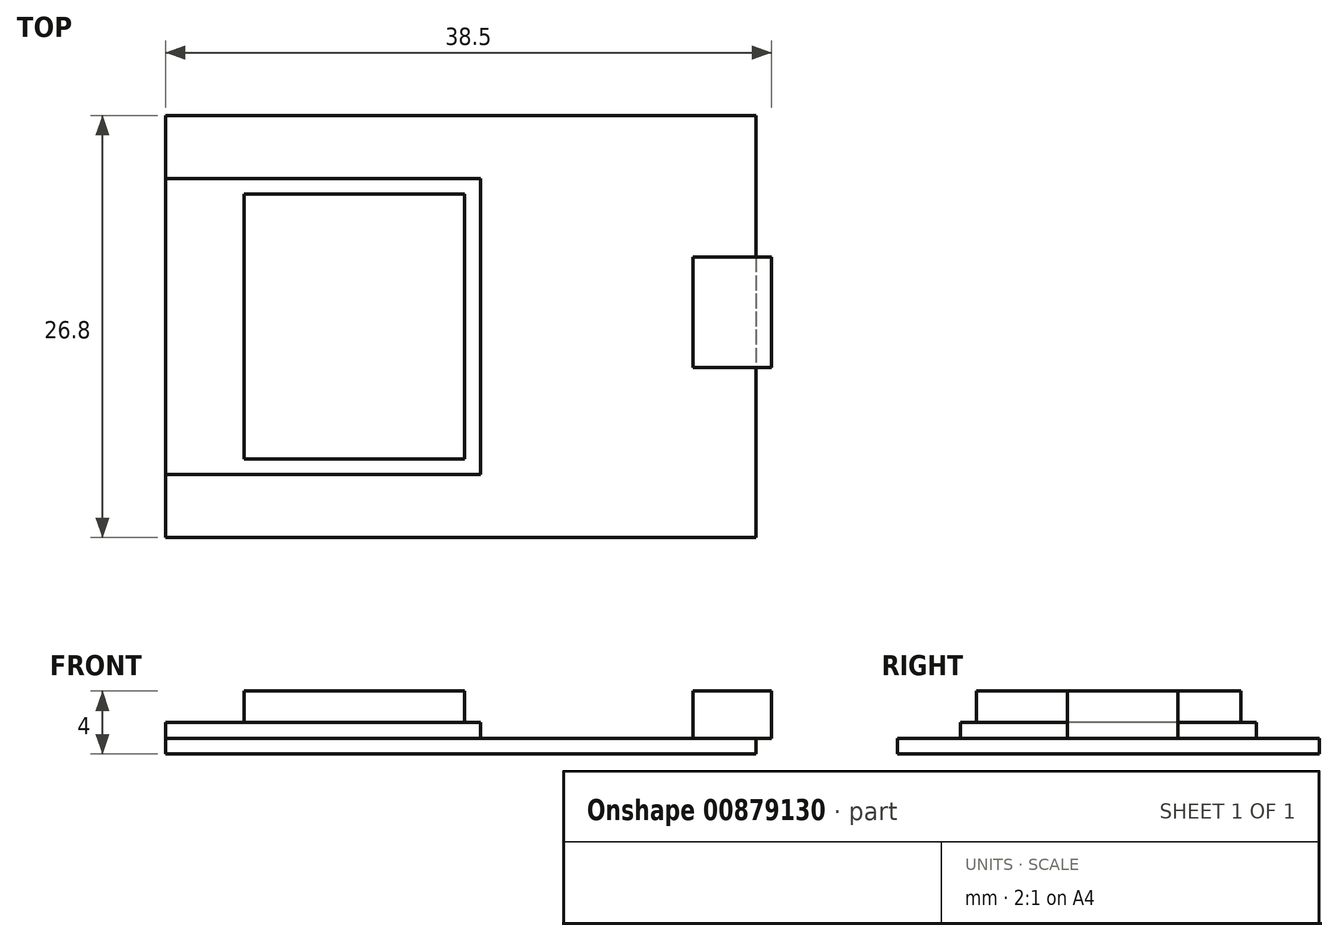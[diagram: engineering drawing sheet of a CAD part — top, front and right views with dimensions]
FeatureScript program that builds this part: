
annotation { "Feature Type Name" : "Feature", "Feature Type Description" : "" }
export const myFeature = defineFeature(function(context is Context, id is Id, definition is map)
    precondition{}
    {
        {
            var Q0;
            Q0=qCreatedBy(makeId("Top.planeOp"),FACE);
            var sketch = newSketch(context, id + "F0", { "sketchPlane" : qUnion([Q0])});
            skLineSegment(sketch, "E0.bottom", {"start": v(0, 26.8) * mm, "end": v(37.5, 26.8) * mm});
            skLineSegment(sketch, "E0.top", {"start": v(0, 0) * mm, "end": v(37.5, 0) * mm});
            skLineSegment(sketch, "E0.left", {"start": v(0, 26.8) * mm, "end": v(0, 0) * mm});
            skLineSegment(sketch, "E0.right", {"start": v(37.5, 26.8) * mm, "end": v(37.5, 0) * mm});
            skSolve(sketch);
        }
        {
            var Q0;
            Q0 = qSketchRegion(id + "F0", true);
            extrude(context, id + "F1", {"entities" : qUnion([Q0]), "depth" : 1 * mm, "offsetDistance" : 25 * mm});
        }
        {
            var Q0;
            Q0=makeQuery(id+"F1.opExtrude","CAP_FACE",FACE,{"disambiguationData":[OSD([sQuery(id+"F0.wireOp",EDGE,"E0.bottom"),sQuery(id+"F0.wireOp",EDGE,"E0.top"),sQuery(id+"F0.wireOp",EDGE,"E0.left"),sQuery(id+"F0.wireOp",EDGE,"E0.right")])],"isStart":false});
            var sketch = newSketch(context, id + "F2", { "sketchPlane" : qUnion([Q0])});
            skLineSegment(sketch, "E1.bottom", {"start": v(33.5, 17.8) * mm, "end": v(38.5, 17.8) * mm});
            skLineSegment(sketch, "E1.top", {"start": v(33.5, 10.8) * mm, "end": v(38.5, 10.8) * mm});
            skLineSegment(sketch, "E1.left", {"start": v(33.5, 17.8) * mm, "end": v(33.5, 10.8) * mm});
            skLineSegment(sketch, "E1.right", {"start": v(38.5, 17.8) * mm, "end": v(38.5, 10.8) * mm});
            skSolve(sketch);
        }
        {
            var Q0;
            Q0 = qSketchRegion(id + "F2", true);
            extrude(context, id + "F3", {"entities" : qUnion([Q0]), "operationType" : NewBodyOperationType.ADD, "depth" : 3 * mm, "offsetDistance" : 25 * mm});
        }
        {
            var Q0;
            Q0=makeQuery(id+"F1.opExtrude","CAP_FACE",FACE,{"disambiguationData":[OSD([sQuery(id+"F0.wireOp",EDGE,"E0.bottom"),sQuery(id+"F0.wireOp",EDGE,"E0.top"),sQuery(id+"F0.wireOp",EDGE,"E0.left"),sQuery(id+"F0.wireOp",EDGE,"E0.right")])],"isStart":false});
            var sketch = newSketch(context, id + "F4", { "sketchPlane" : qUnion([Q0])});
            skLineSegment(sketch, "E2.bottom", {"start": v(0, 22.8) * mm, "end": v(20, 22.8) * mm});
            skLineSegment(sketch, "E2.top", {"start": v(0, 4) * mm, "end": v(20, 4) * mm});
            skLineSegment(sketch, "E2.left", {"start": v(0, 22.8) * mm, "end": v(0, 4) * mm});
            skLineSegment(sketch, "E2.right", {"start": v(20, 22.8) * mm, "end": v(20, 4) * mm});
            skSolve(sketch);
        }
        {
            var Q0;
            Q0 = qSketchRegion(id + "F4", true);
            extrude(context, id + "F5", {"entities" : qUnion([Q0]), "operationType" : NewBodyOperationType.ADD, "depth" : 1 * mm, "offsetDistance" : 25 * mm});
        }
        {
            var Q0;
            Q0=makeQuery(id+"F5.opExtrude","CAP_FACE",FACE,{"disambiguationData":[OSD([sQuery(id+"F4.wireOp",EDGE,"E2.bottom"),sQuery(id+"F4.wireOp",EDGE,"E2.top"),sQuery(id+"F4.wireOp",EDGE,"E2.left"),sQuery(id+"F4.wireOp",EDGE,"E2.right")])],"isStart":false});
            var sketch = newSketch(context, id + "F6", { "sketchPlane" : qUnion([Q0])});
            skLineSegment(sketch, "E3.bottom", {"start": v(5, 21.8) * mm, "end": v(19, 21.8) * mm});
            skLineSegment(sketch, "E3.top", {"start": v(5, 5) * mm, "end": v(19, 5) * mm});
            skLineSegment(sketch, "E3.left", {"start": v(5, 21.8) * mm, "end": v(5, 5) * mm});
            skLineSegment(sketch, "E3.right", {"start": v(19, 21.8) * mm, "end": v(19, 5) * mm});
            skSolve(sketch);
        }
        {
            var Q0;
            Q0 = qSketchRegion(id + "F6", true);
            extrude(context, id + "F7", {"entities" : qUnion([Q0]), "operationType" : NewBodyOperationType.ADD, "depth" : 2 * mm, "offsetDistance" : 25 * mm});
        }
        {
            var Q0;
            Q0 = qSketchRegion(id + "F6", true);
            extrude(context, id + "F8", {"entities" : qUnion([Q0]), "operationType" : NewBodyOperationType.ADD, "depth" : 2 * mm, "offsetDistance" : 25 * mm});
        }
    });
